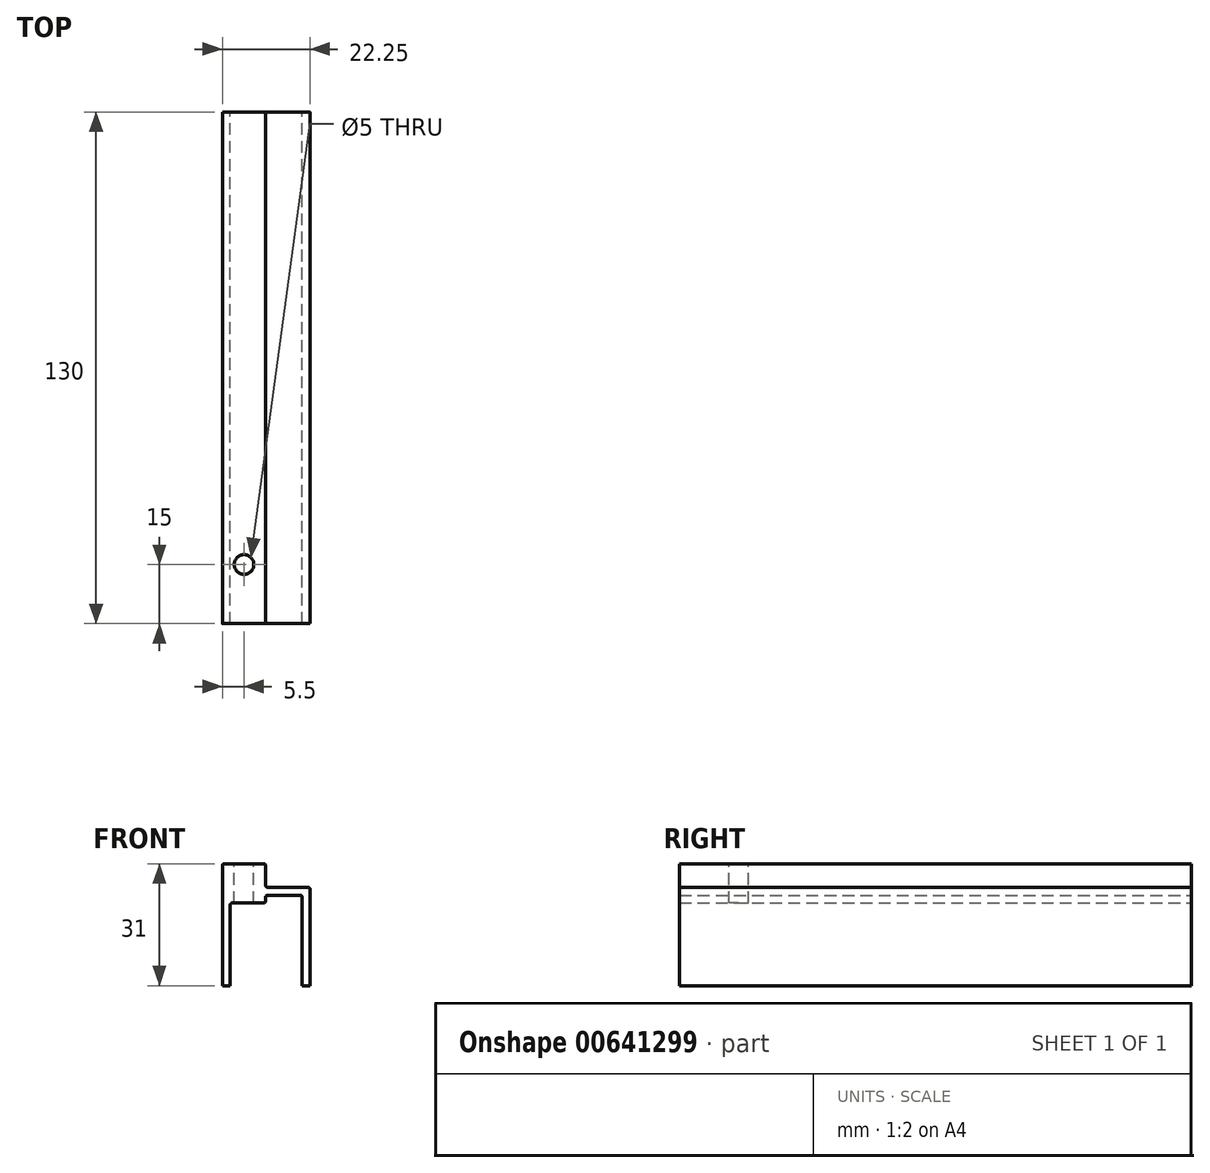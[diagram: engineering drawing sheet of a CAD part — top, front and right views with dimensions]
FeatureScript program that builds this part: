
annotation { "Feature Type Name" : "Feature", "Feature Type Description" : "" }
export const myFeature = defineFeature(function(context is Context, id is Id, definition is map)
    precondition{}
    {
        {
            var Q0;
            Q0=qCreatedBy(makeId("Front.planeOp"),FACE);
            var sketch = newSketch(context, id + "F0", { "sketchPlane" : qUnion([Q0])});
            skLineSegment(sketch, "E0", {"start": v(0, 0) * mm, "end": v(0, 24.5) * mm});
            skArc(sketch, "E1", {"start": v(0, 24.5) * mm, "mid": v(-0.15, 24.85) * mm, "end": v(-0.5, 25) * mm});
            skLineSegment(sketch, "E2", {"start": v(-2, 0) * mm, "end": v(-2, 22.5) * mm});
            skArc(sketch, "E3", {"start": v(-2, 22.5) * mm, "mid": v(-2.15, 22.85) * mm, "end": v(-2.5, 23) * mm});
            skLineSegment(sketch, "E4", {"start": v(-20.25, 20.5) * mm, "end": v(-20.25, 0) * mm});
            skLineSegment(sketch, "E5", {"start": v(-22.25, 0) * mm, "end": v(-22.25, 22.5) * mm});
            skArc(sketch, "E6", {"start": v(-10.75, 23) * mm, "mid": v(-11.1, 22.85) * mm, "end": v(-11.25, 22.5) * mm});
            skLineSegment(sketch, "E7", {"start": v(-11.25, 22.5) * mm, "end": v(-11.25, 21.5) * mm});
            skLineSegment(sketch, "E8", {"start": v(-0.5, 25) * mm, "end": v(-10.75, 25) * mm});
            skArc(sketch, "E9", {"start": v(-11.75, 21) * mm, "mid": v(-11.4, 21.15) * mm, "end": v(-11.25, 21.5) * mm});
            skLineSegment(sketch, "E10", {"start": v(-11.75, 21) * mm, "end": v(-19.75, 21) * mm});
            skLineSegment(sketch, "E11", {"start": v(-22.25, 0) * mm, "end": v(-20.25, 0) * mm});
            skLineSegment(sketch, "E12", {"start": v(-2, 0) * mm, "end": v(0, 0) * mm});
            skArc(sketch, "E13", {"start": v(-11.25, 25.5) * mm, "mid": v(-11.1, 25.15) * mm, "end": v(-10.75, 25) * mm});
            skArc(sketch, "E14", {"start": v(-11.25, 30.5) * mm, "mid": v(-11.4, 30.85) * mm, "end": v(-11.75, 31) * mm});
            skArc(sketch, "E15", {"start": v(-21.75, 31) * mm, "mid": v(-22.1, 30.85) * mm, "end": v(-22.25, 30.5) * mm});
            skLineSegment(sketch, "E16", {"start": v(-21.75, 31) * mm, "end": v(-11.75, 31) * mm});
            skLineSegment(sketch, "E17", {"start": v(-11.25, 30.5) * mm, "end": v(-11.25, 25.5) * mm});
            skLineSegment(sketch, "E18", {"start": v(-2.5, 23) * mm, "end": v(-10.75, 23) * mm});
            skArc(sketch, "E19", {"start": v(-19.75, 21) * mm, "mid": v(-20.1, 20.85) * mm, "end": v(-20.25, 20.5) * mm});
            skLineSegment(sketch, "E20", {"start": v(-22.25, 30.5) * mm, "end": v(-22.25, 22.5) * mm});
            skLineSegment(sketch, "E21", {"start": v(-22.25, 22.5) * mm, "end": v(-11.25, 22.5) * mm, "construction": true});
            skLineSegment(sketch, "E22", {"start": v(-11.25, 25.5) * mm, "end": v(-11.25, 22.5) * mm, "construction": true});
            skLineSegment(sketch, "E23", {"start": v(-6.27, 25) * mm, "end": v(-6.27, 23) * mm, "construction": true});
            skLineSegment(sketch, "E24", {"start": v(-16.75, 31) * mm, "end": v(-16.75, 20.46) * mm, "construction": true});
            skPoint(sketch, "E24.endSnap0", {"position": v(-16.75, 22.5) * mm});
            skSolve(sketch);
        }
        {
            var Q0;
            Q0=qSketchRegion(id+"F0",true);
            extrude(context, id + "F1", {"entities" : qUnion([Q0]), "depth" : 130 * mm, "offsetDistance" : 25 * mm});
        }
        {
            var Q0;
            Q0=makeQuery(id+"F1.opExtrude","SWEPT_FACE",FACE,{"disambiguationData":[OSD([sQuery(id+"F0.wireOp",EDGE,"E16")])]});
            var sketch = newSketch(context, id + "F2", { "sketchPlane" : qUnion([Q0])});
            skPoint(sketch, "E25", {"position": v(-16.75, -115) * mm});
            skSolve(sketch);
        }
        {
            var Q0;
            Q0=sQuery(id+"F2.wireOp",VERTEX,"E25");
            var Q1;
            Q1=makeQuery(id+"F1.opExtrude","SWEPT_BODY",BODY,{"disambiguationData":[OSD([sQuery(id+"F0.wireOp",EDGE,"E0"),sQuery(id+"F0.wireOp",EDGE,"E1"),sQuery(id+"F0.wireOp",EDGE,"E2"),sQuery(id+"F0.wireOp",EDGE,"E3"),sQuery(id+"F0.wireOp",EDGE,"E4"),sQuery(id+"F0.wireOp",EDGE,"E5"),sQuery(id+"F0.wireOp",EDGE,"E6"),sQuery(id+"F0.wireOp",EDGE,"E7"),sQuery(id+"F0.wireOp",EDGE,"E8"),sQuery(id+"F0.wireOp",EDGE,"E9"),sQuery(id+"F0.wireOp",EDGE,"E10"),sQuery(id+"F0.wireOp",EDGE,"E11"),sQuery(id+"F0.wireOp",EDGE,"E12"),sQuery(id+"F0.wireOp",EDGE,"E13"),sQuery(id+"F0.wireOp",EDGE,"E14"),sQuery(id+"F0.wireOp",EDGE,"E15"),sQuery(id+"F0.wireOp",EDGE,"E16"),sQuery(id+"F0.wireOp",EDGE,"E17"),sQuery(id+"F0.wireOp",EDGE,"E18"),sQuery(id+"F0.wireOp",EDGE,"E19"),sQuery(id+"F0.wireOp",EDGE,"E20")])]});
            hole(context, id + "F3", {"style" : HoleStyle.SIMPLE, "endStyle" : HoleEndStyle.THROUGH, "holeDiameter" : 5 * mm, "majorDiameter" : 5 * mm, "isTappedThrough" : true, "tappedDepth" : 12 * mm, "tapClearance" : 3, "locations" : qUnion([Q0]), "scope" : qUnion([Q1])});
        }
    });
